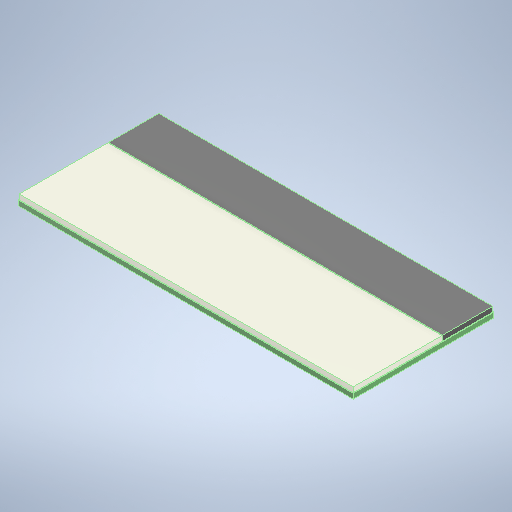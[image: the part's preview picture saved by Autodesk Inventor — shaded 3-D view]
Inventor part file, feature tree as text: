
AUTODESK INVENTOR PART (.ipt)
format: ipt  version: 2025.3 (Build 293356000, 356)  size: 247,296 bytes
history: native  units: mm
features: extrude x2, sketch x2, other x1
ambient origin geometry x8: Origin, YZ Plane, XZ Plane, XY Plane, X Axis, Y Axis, Z Axis, Center Point
bodies: Body1 (feature_tree)
feature tree (5):
  other  "ソリッド1"
  extrude  "押し出し1"  Depth=66.0mm
  extrude  "押し出し4"  Depth=27.7mm
  sketch  "スケッチ1"
  sketch  "スケッチ5"
